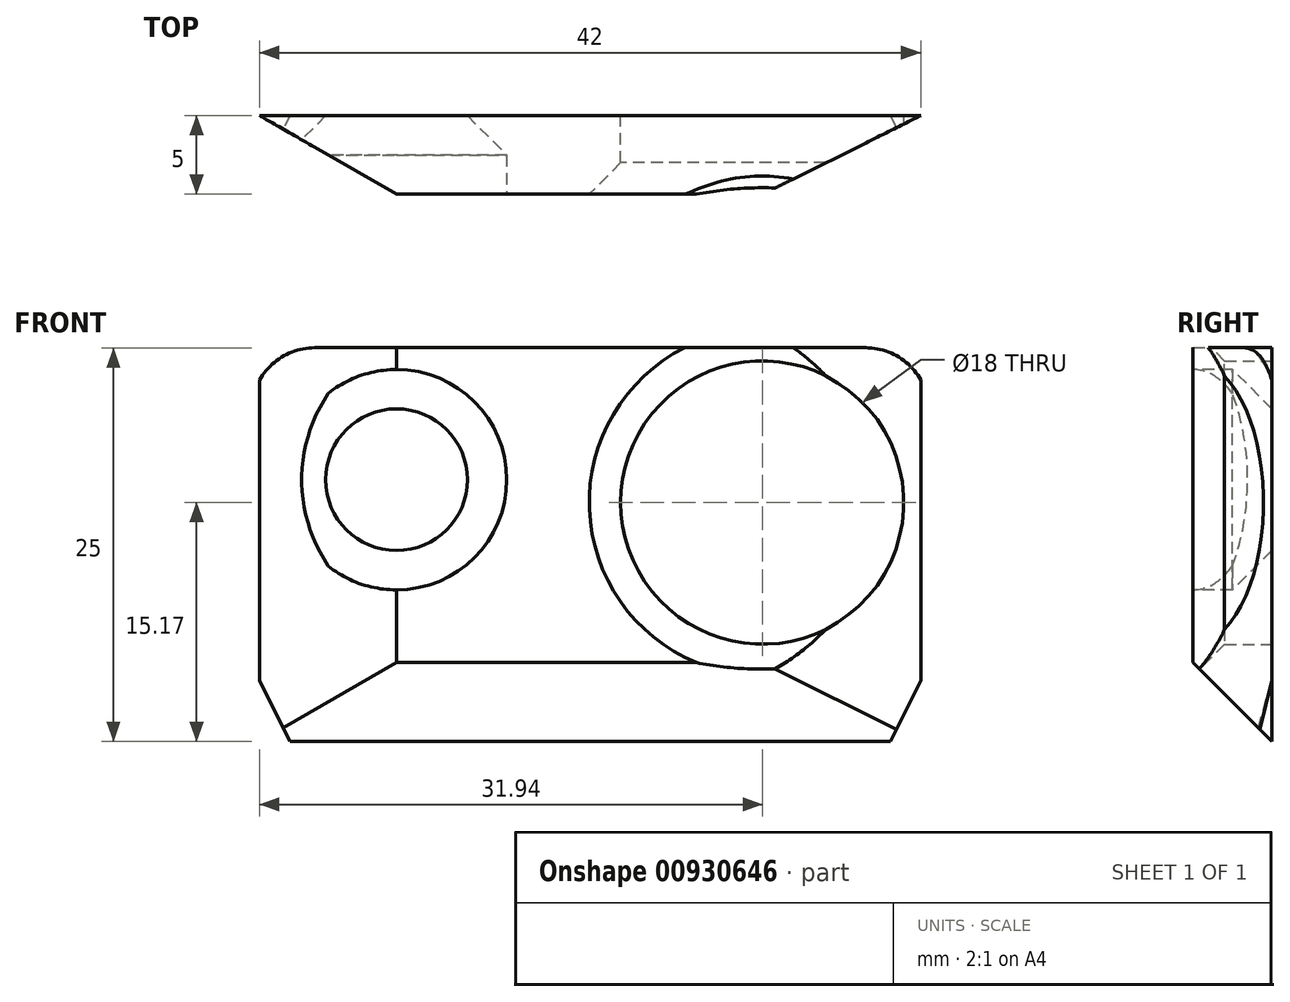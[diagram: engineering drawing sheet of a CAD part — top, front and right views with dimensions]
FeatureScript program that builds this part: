
annotation { "Feature Type Name" : "Feature", "Feature Type Description" : "" }
export const myFeature = defineFeature(function(context is Context, id is Id, definition is map)
    precondition{}
    {
        {
            var Q0;
            Q0=qCreatedBy(makeId("Front.planeOp"),FACE);
            var sketch = newSketch(context, id + "F0", { "sketchPlane" : qUnion([Q0])});
            skLineSegment(sketch, "E0", {"start": v(-22, 0) * mm, "end": v(-22, 25.38) * mm, "construction": true});
            skLineSegment(sketch, "E1", {"start": v(-22, 25.38) * mm, "end": v(22, 25.38) * mm, "construction": true});
            skLineSegment(sketch, "E2", {"start": v(22, 25.38) * mm, "end": v(22, 0) * mm, "construction": true});
            skLineSegment(sketch, "E3", {"start": v(22, 0) * mm, "end": v(19.7, -4.62) * mm, "construction": true});
            skLineSegment(sketch, "E4", {"start": v(19.7, -4.62) * mm, "end": v(-19.7, -4.62) * mm, "construction": true});
            skLineSegment(sketch, "E5", {"start": v(-19.7, -4.62) * mm, "end": v(-22, 0) * mm, "construction": true});
            skCircle(sketch, "E6", {"center": v(-12.3, 13) * mm, "radius": 4 * mm, "construction": true});
            skCircle(sketch, "E7", {"center": v(10.94, 11.55) * mm, "radius": 8.5 * mm, "construction": true});
            skCircle(sketch, "E8", {"center": v(0.1, 2.5) * mm, "radius": 0.9 * mm, "construction": true});
            skCircle(sketch, "E9", {"center": v(0.1, 23.5) * mm, "radius": 0.9 * mm, "construction": true});
            skCircle(sketch, "E10", {"center": v(-12.4, 23.5) * mm, "radius": 0.9 * mm, "construction": true});
            skCircle(sketch, "E11", {"center": v(-12.4, 2.5) * mm, "radius": 0.9 * mm, "construction": true});
            skCircle(sketch, "E12", {"center": v(17.24, 20.06) * mm, "radius": 1.4 * mm, "construction": true});
            skCircle(sketch, "E13", {"center": v(4.64, 3.04) * mm, "radius": 1.4 * mm, "construction": true});
            skLineSegment(sketch, "E14", {"start": v(-17.5, 22.38) * mm, "end": v(17.5, 22.38) * mm, "construction": true});
            skArc(sketch, "E15", {"start": v(-17.5, 22.38) * mm, "mid": v(-20.16, 21.62) * mm, "end": v(-22, 19.56) * mm, "construction": true});
            skArc(sketch, "E16", {"start": v(22, 19.56) * mm, "mid": v(20.16, 21.62) * mm, "end": v(17.5, 22.38) * mm, "construction": true});
            skSolve(sketch);
        }
        {
            var Q0;
            Q0=qCreatedBy(makeId("Front.planeOp"),FACE);
            var sketch = newSketch(context, id + "F1", { "sketchPlane" : qUnion([Q0])});
            skLineSegment(sketch, "E17", {"start": v(-21, 19.32) * mm, "end": v(-21, 0.24) * mm});
            skLineSegment(sketch, "E18", {"start": v(21, 19.32) * mm, "end": v(21, 0.24) * mm});
            skLineSegment(sketch, "E19", {"start": v(-17.5, 21.38) * mm, "end": v(17.5, 21.38) * mm});
            skLineSegment(sketch, "E20", {"start": v(-19.07, -3.62) * mm, "end": v(19.07, -3.62) * mm});
            skCircle(sketch, "E21", {"center": v(-12.3, 13) * mm, "radius": 4.5 * mm});
            skCircle(sketch, "E22", {"center": v(10.94, 11.55) * mm, "radius": 9 * mm});
            skLineSegment(sketch, "E23", {"start": v(-21, 0.24) * mm, "end": v(-19.07, -3.62) * mm});
            skLineSegment(sketch, "E24", {"start": v(19.07, -3.62) * mm, "end": v(21, 0.24) * mm});
            skArc(sketch, "E25", {"start": v(-17.5, 21.38) * mm, "mid": v(-19.53, 20.83) * mm, "end": v(-21, 19.32) * mm});
            skArc(sketch, "E26", {"start": v(21, 19.32) * mm, "mid": v(19.53, 20.83) * mm, "end": v(17.5, 21.38) * mm});
            skSolve(sketch);
        }
        {
            var Q0;
            Q0=qSketchRegion(id+"F1",true);
            extrude(context, id + "F2", {"entities" : qUnion([Q0]), "depth" : 5 * mm, "offsetDistance" : 25 * mm});
        }
        {
            var Q0;
            Q0=makeQuery(id+"F2.opExtrude","CAP_FACE",FACE,{"disambiguationData":[OSD([sQuery(id+"F1.wireOp",EDGE,"E17"),sQuery(id+"F1.wireOp",EDGE,"E18"),sQuery(id+"F1.wireOp",EDGE,"E19"),sQuery(id+"F1.wireOp",EDGE,"bUA0DR8L-BFFz-R4tk-PDLL-wZLGQbPptVzk"),sQuery(id+"F1.wireOp",EDGE,"YoHFbzKo-LuzB-0cCO-TyFW-VdCM1OG1Tsm7"),sQuery(id+"F1.wireOp",EDGE,"DZbRkJJH-JIrT-eXMR-YIdL-7dBeNxE0hC4q"),sQuery(id+"F1.wireOp",EDGE,"E20"),sQuery(id+"F1.wireOp",EDGE,"paGs54OP-qBYp-fpE7-8fXg-RC5dLIZwy8cC"),sQuery(id+"F1.wireOp",EDGE,"E21"),sQuery(id+"F1.wireOp",EDGE,"E22")])],"isStart":false});
            var sketch = newSketch(context, id + "F3", { "sketchPlane" : qUnion([Q0])});
            skCircle(sketch, "E27", {"center": v(-12.3, 13) * mm, "radius": 7 * mm});
            skSolve(sketch);
        }
        {
            var Q0;
            Q0=qSketchRegion(id+"F3",true);
            extrude(context, id + "F4", {"entities" : qUnion([Q0]), "operationType" : NewBodyOperationType.REMOVE, "oppositeDirection" : true, "depth" : 2 * mm, "offsetDistance" : 25 * mm});
        }
        {
            var Q0;
            Q0=makeQuery(id+"F2.opExtrude","CAP_EDGE",EDGE,{"disambiguationData":[OSD([sQuery(id+"F1.wireOp",EDGE,"E22")])],"isStart":false});
            chamfer(context, id + "F5", {"entities" : qUnion([Q0]), "width" : 2 * mm, "tangentPropagation" : true});
        }
        {
            var Q0;
            Q0=makeQuery(id+"F4.boolean.opBoolean","INTERSECT",EDGE,{"derivedFrom":[makeQuery(id+"F2.opExtrude","SWEPT_FACE",FACE,{"disambiguationData":[OSD([sQuery(id+"F1.wireOp",EDGE,"E21")])]}),makeQuery(id+"F4.opExtrude","CAP_FACE",FACE,{"disambiguationData":[OSD([sQuery(id+"F3.wireOp",EDGE,"E27")])],"isStart":false})]});
            chamfer(context, id + "F6", {"entities" : qUnion([Q0]), "width" : 3 * mm, "tangentPropagation" : true});
        }
        {
            var Q0;
            Q0=makeQuery(id+"F2.opExtrude","SWEPT_FACE",FACE,{"disambiguationData":[OSD([sQuery(id+"F1.wireOp",EDGE,"E20")])]});
            var sketch = newSketch(context, id + "F7", { "sketchPlane" : qUnion([Q0])});
            skLineSegment(sketch, "E28", {"start": v(-21, 0) * mm, "end": v(-12.3, 5) * mm});
            skLineSegment(sketch, "E29", {"start": v(-12.3, 5) * mm, "end": v(-21, 5) * mm});
            skLineSegment(sketch, "E30", {"start": v(-21, 5) * mm, "end": v(-21, 0) * mm});
            skLineSegment(sketch, "E31", {"start": v(10.94, 5) * mm, "end": v(21, 0) * mm});
            skLineSegment(sketch, "E32", {"start": v(21, 0) * mm, "end": v(21, 5) * mm});
            skLineSegment(sketch, "E33", {"start": v(21, 5) * mm, "end": v(10.94, 5) * mm});
            skSolve(sketch);
        }
        {
            var Q0;
            Q0=qSketchRegion(id+"F7",true);
            var Q1;
            Q1=makeQuery(id+"F2.opExtrude","SWEPT_FACE",FACE,{"disambiguationData":[OSD([sQuery(id+"F1.wireOp",EDGE,"E19")])]});
            extrude(context, id + "F8", {"entities" : qUnion([Q0]), "operationType" : NewBodyOperationType.REMOVE, "endBound" : BoundingType.UP_TO_SURFACE, "oppositeDirection" : true, "depth" : 25 * mm, "endBoundEntityFace" : qUnion([Q1]), "offsetDistance" : 25 * mm});
        }
        {
            var Q0;
            Q0=qCreatedBy(makeId("Right.planeOp"),FACE);
            cPlane(context, id + "F9", {"entities" : qUnion([Q0]), "cplaneType" : CPlaneType.OFFSET, "offset" : 21 * mm, "width" : 150 * mm, "height" : 150 * mm});
        }
        {
            var Q0;
            Q0=qCreatedBy(id+"F9.planeOp",FACE);
            var sketch = newSketch(context, id + "F10", { "sketchPlane" : qUnion([Q0])});
            skLineSegment(sketch, "E34", {"start": v(0, -3.62) * mm, "end": v(-5, 1.38) * mm});
            skLineSegment(sketch, "E35", {"start": v(-5, 1.38) * mm, "end": v(-5, -3.62) * mm});
            skLineSegment(sketch, "E36", {"start": v(0, -3.62) * mm, "end": v(-5, -3.62) * mm});
            skSolve(sketch);
        }
        {
            var Q0;
            Q0=qSketchRegion(id+"F10",true);
            var Q1;
            Q1=makeQuery(id+"F8.boolean.opBoolean","COPY",FACE,{"derivedFrom":makeQuery(id+"F8.opExtrude","SWEPT_FACE",FACE,{"disambiguationData":[OSD([sQuery(id+"F7.wireOp",EDGE,"E28")])]})});
            extrude(context, id + "F11", {"entities" : qUnion([Q0]), "operationType" : NewBodyOperationType.REMOVE, "endBound" : BoundingType.UP_TO_SURFACE, "oppositeDirection" : true, "depth" : 42 * mm, "endBoundEntityFace" : qUnion([Q1]), "offsetDistance" : 25 * mm});
        }
    });
